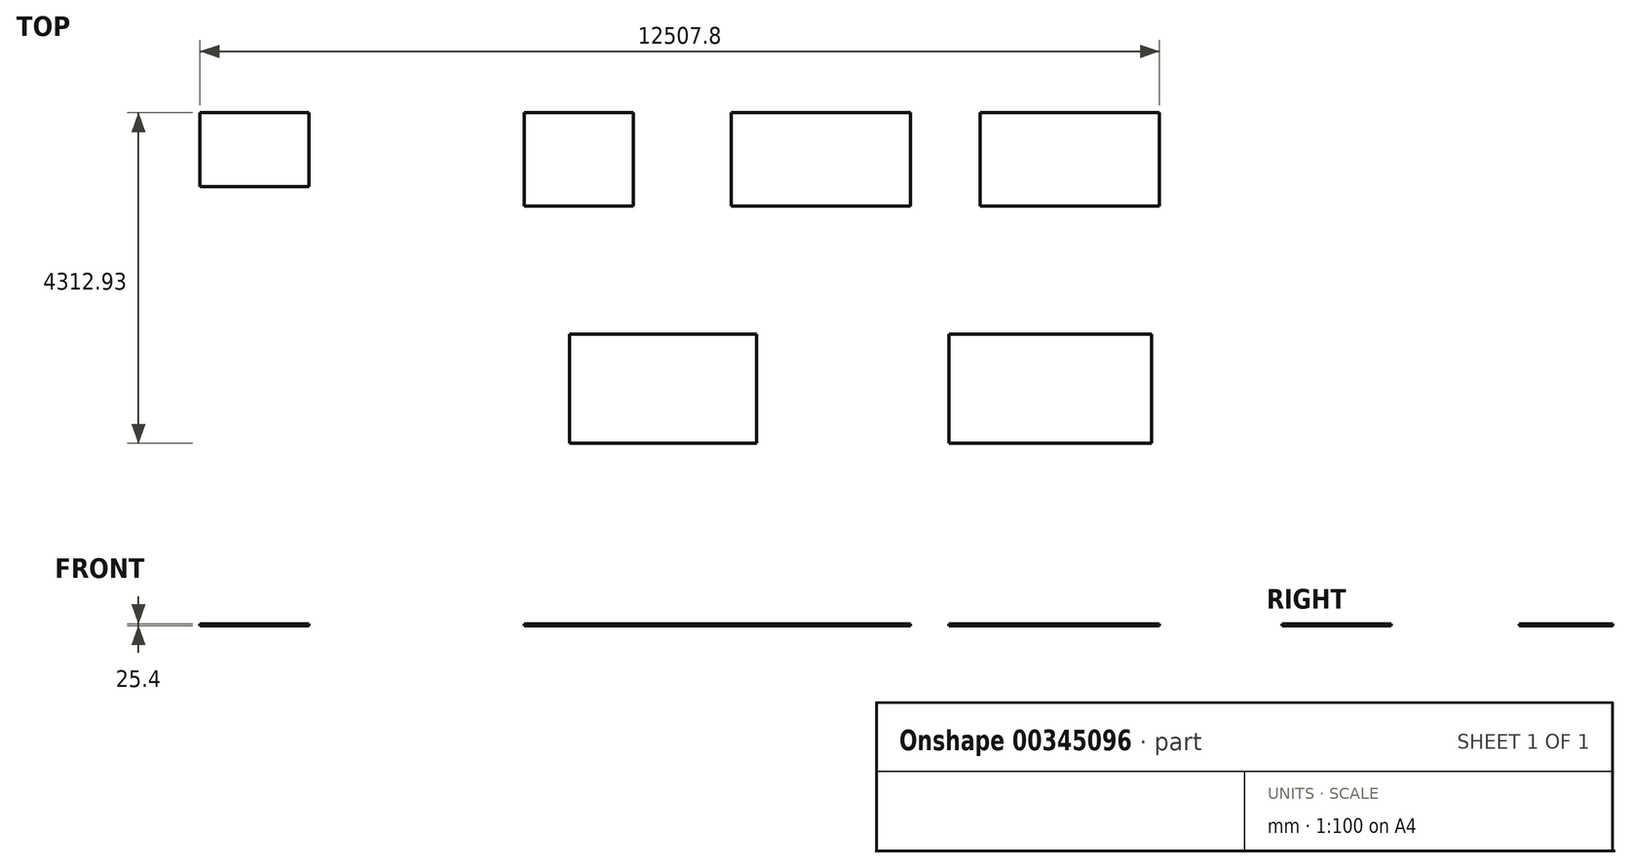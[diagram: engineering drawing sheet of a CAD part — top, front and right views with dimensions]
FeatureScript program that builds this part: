
annotation { "Feature Type Name" : "Feature", "Feature Type Description" : "" }
export const myFeature = defineFeature(function(context is Context, id is Id, definition is map)
    precondition{}
    {
        {
            var Q0;
            Q0=qCreatedBy(makeId("Top.planeOp"),FACE);
            var sketch = newSketch(context, id + "F0", { "sketchPlane" : qUnion([Q0])});
            skLineSegment(sketch, "E0.bottom", {"start": v(-2087.2, 1219.2) * mm, "end": v(351.2, 1219.2) * mm, "construction": true});
            skLineSegment(sketch, "E0.top", {"start": v(-2087.2, 0) * mm, "end": v(351.2, 0) * mm, "construction": true});
            skLineSegment(sketch, "E0.left", {"start": v(-2087.2, 1219.2) * mm, "end": v(-2087.2, 0) * mm, "construction": true});
            skLineSegment(sketch, "E0.right", {"start": v(351.2, 1219.2) * mm, "end": v(351.2, 0) * mm, "construction": true});
            skLineSegment(sketch, "E1.bottom", {"start": v(-2493.6, -1671.33) * mm, "end": v(351.2, -1671.33) * mm, "construction": true});
            skLineSegment(sketch, "E1.top", {"start": v(-2493.6, -3093.73) * mm, "end": v(351.2, -3093.73) * mm, "construction": true});
            skLineSegment(sketch, "E1.left", {"start": v(-2493.6, -1671.33) * mm, "end": v(-2493.6, -3093.73) * mm, "construction": true});
            skLineSegment(sketch, "E1.right", {"start": v(351.2, -1671.33) * mm, "end": v(351.2, -3093.73) * mm, "construction": true});
            skLineSegment(sketch, "E2", {"start": v(-1369.66, -1671.33) * mm, "end": v(-1369.66, -3093.73) * mm, "construction": true});
            skLineSegment(sketch, "E3.bottom", {"start": v(-2493.6, -1671.33) * mm, "end": v(-1274.4, -1671.33) * mm});
            skLineSegment(sketch, "E3.top", {"start": v(-2493.6, -3093.73) * mm, "end": v(-1274.4, -3093.73) * mm});
            skLineSegment(sketch, "E3.left", {"start": v(-2493.6, -1671.33) * mm, "end": v(-2493.6, -3093.73) * mm});
            skLineSegment(sketch, "E3.right", {"start": v(-1274.4, -1671.33) * mm, "end": v(-1274.4, -3093.73) * mm});
            skLineSegment(sketch, "E4.bottom", {"start": v(-2087.2, 1219.2) * mm, "end": v(-664.8, 1219.2) * mm});
            skLineSegment(sketch, "E4.top", {"start": v(-2087.2, 0) * mm, "end": v(-664.8, 0) * mm});
            skLineSegment(sketch, "E4.left", {"start": v(-2087.2, 1219.2) * mm, "end": v(-2087.2, 0) * mm});
            skLineSegment(sketch, "E4.right", {"start": v(-664.8, 1219.2) * mm, "end": v(-664.8, 0) * mm});
            skLineSegment(sketch, "E5.bottom", {"start": v(-7440.47, -1671.33) * mm, "end": v(-4036.87, -1671.33) * mm, "construction": true});
            skLineSegment(sketch, "E5.top", {"start": v(-7440.47, -3093.73) * mm, "end": v(-4036.87, -3093.73) * mm, "construction": true});
            skLineSegment(sketch, "E5.left", {"start": v(-7440.47, -1671.33) * mm, "end": v(-7440.47, -3093.73) * mm, "construction": true});
            skLineSegment(sketch, "E5.right", {"start": v(-4036.87, -1671.33) * mm, "end": v(-4036.87, -3093.73) * mm, "construction": true});
            skLineSegment(sketch, "E6.bottom", {"start": v(-2895.85, 1219.2) * mm, "end": v(-5334.25, 1219.2) * mm, "construction": true});
            skLineSegment(sketch, "E6.top", {"start": v(-2895.85, 0) * mm, "end": v(-5334.25, 0) * mm, "construction": true});
            skLineSegment(sketch, "E6.left", {"start": v(-2895.85, 1219.2) * mm, "end": v(-2895.85, 0) * mm, "construction": true});
            skLineSegment(sketch, "E6.right", {"start": v(-5334.25, 1219.2) * mm, "end": v(-5334.25, 0) * mm, "construction": true});
            skLineSegment(sketch, "E7.bottom", {"start": v(-5334.25, 1219.2) * mm, "end": v(-3911.85, 1219.2) * mm});
            skLineSegment(sketch, "E7.top", {"start": v(-5334.25, 0) * mm, "end": v(-3911.85, 0) * mm});
            skLineSegment(sketch, "E7.left", {"start": v(-5334.25, 1219.2) * mm, "end": v(-5334.25, 0) * mm});
            skLineSegment(sketch, "E7.right", {"start": v(-3911.85, 1219.2) * mm, "end": v(-3911.85, 0) * mm});
            skLineSegment(sketch, "E8.bottom", {"start": v(-7440.47, -1671.33) * mm, "end": v(-6221.27, -1671.33) * mm});
            skLineSegment(sketch, "E8.top", {"start": v(-7440.47, -3093.73) * mm, "end": v(-6221.27, -3093.73) * mm});
            skLineSegment(sketch, "E8.left", {"start": v(-7440.47, -1671.33) * mm, "end": v(-7440.47, -3093.73) * mm});
            skLineSegment(sketch, "E8.right", {"start": v(-6221.27, -1671.33) * mm, "end": v(-6221.27, -3093.73) * mm});
            skLineSegment(sketch, "E9.bottom", {"start": v(-3911.85, 1219.2) * mm, "end": v(-3200.65, 1219.2) * mm});
            skLineSegment(sketch, "E9.top", {"start": v(-3911.85, 0) * mm, "end": v(-3200.65, 0) * mm});
            skLineSegment(sketch, "E9.right", {"start": v(-3200.65, 1219.2) * mm, "end": v(-3200.65, 0) * mm});
            skLineSegment(sketch, "E10.bottom", {"start": v(-6221.27, -1671.33) * mm, "end": v(-5002.07, -1671.33) * mm});
            skLineSegment(sketch, "E10.top", {"start": v(-6221.27, -2382.53) * mm, "end": v(-5002.07, -2382.53) * mm});
            skLineSegment(sketch, "E10.left", {"start": v(-6221.27, -1671.33) * mm, "end": v(-6221.27, -2382.53) * mm});
            skLineSegment(sketch, "E10.right", {"start": v(-5002.07, -1671.33) * mm, "end": v(-5002.07, -2382.53) * mm});
            skLineSegment(sketch, "E11.top", {"start": v(-6221.27, -3093.73) * mm, "end": v(-5002.07, -3093.73) * mm});
            skLineSegment(sketch, "E11.left", {"start": v(-6221.27, -2382.53) * mm, "end": v(-6221.27, -3093.73) * mm});
            skLineSegment(sketch, "E11.right", {"start": v(-5002.07, -2382.53) * mm, "end": v(-5002.07, -3093.73) * mm});
            skLineSegment(sketch, "E12.bottom", {"start": v(-664.8, 1219.2) * mm, "end": v(46.4, 1219.2) * mm});
            skLineSegment(sketch, "E12.top", {"start": v(-664.8, 0) * mm, "end": v(46.4, 0) * mm});
            skLineSegment(sketch, "E12.right", {"start": v(46.4, 1219.2) * mm, "end": v(46.4, 0) * mm});
            skLineSegment(sketch, "E13.bottom", {"start": v(-5590.97, 1219.2) * mm, "end": v(-8029.37, 1219.2) * mm, "construction": true});
            skLineSegment(sketch, "E13.top", {"start": v(-5590.97, 0) * mm, "end": v(-8029.37, 0) * mm, "construction": true});
            skLineSegment(sketch, "E13.left", {"start": v(-5590.97, 1219.2) * mm, "end": v(-5590.97, 0) * mm, "construction": true});
            skLineSegment(sketch, "E13.right", {"start": v(-8029.37, 1219.2) * mm, "end": v(-8029.37, 0) * mm, "construction": true});
            skLineSegment(sketch, "E14.bottom", {"start": v(-8029.37, 1219.2) * mm, "end": v(-6606.97, 1219.2) * mm});
            skLineSegment(sketch, "E14.top", {"start": v(-8029.37, 0) * mm, "end": v(-6606.97, 0) * mm});
            skLineSegment(sketch, "E14.left", {"start": v(-8029.37, 1219.2) * mm, "end": v(-8029.37, 0) * mm});
            skLineSegment(sketch, "E14.right", {"start": v(-6606.97, 1219.2) * mm, "end": v(-6606.97, 0) * mm});
            skLineSegment(sketch, "E15.bottom", {"start": v(-1274.4, -1671.33) * mm, "end": v(148, -1671.33) * mm});
            skLineSegment(sketch, "E15.top", {"start": v(-1274.4, -3093.73) * mm, "end": v(148, -3093.73) * mm});
            skLineSegment(sketch, "E15.right", {"start": v(148, -1671.33) * mm, "end": v(148, -3093.73) * mm});
            skLineSegment(sketch, "E16.bottom", {"start": v(-9819.8, 1219.2) * mm, "end": v(-12258.2, 1219.2) * mm, "construction": true});
            skLineSegment(sketch, "E16.top", {"start": v(-9819.8, 0) * mm, "end": v(-12258.2, 0) * mm, "construction": true});
            skLineSegment(sketch, "E16.left", {"start": v(-9819.8, 1219.2) * mm, "end": v(-9819.8, 0) * mm, "construction": true});
            skLineSegment(sketch, "E16.right", {"start": v(-12258.2, 1219.2) * mm, "end": v(-12258.2, 0) * mm, "construction": true});
            skLineSegment(sketch, "E17.bottom", {"start": v(-12258.2, 1219.2) * mm, "end": v(-10835.8, 1219.2) * mm});
            skLineSegment(sketch, "E17.top", {"start": v(-12258.2, 254) * mm, "end": v(-10835.8, 254) * mm});
            skLineSegment(sketch, "E17.left", {"start": v(-12258.2, 1219.2) * mm, "end": v(-12258.2, 254) * mm});
            skLineSegment(sketch, "E17.right", {"start": v(-10835.8, 1219.2) * mm, "end": v(-10835.8, 254) * mm});
            skLineSegment(sketch, "E18.bottom", {"start": v(-3200.65, 1219.2) * mm, "end": v(-2997.45, 1219.2) * mm});
            skLineSegment(sketch, "E18.top", {"start": v(-3200.65, 0) * mm, "end": v(-2997.45, 0) * mm});
            skLineSegment(sketch, "E18.right", {"start": v(-2997.45, 1219.2) * mm, "end": v(-2997.45, 0) * mm});
            skLineSegment(sketch, "E19.bottom", {"start": v(46.4, 1219.2) * mm, "end": v(249.6, 1219.2) * mm});
            skLineSegment(sketch, "E19.top", {"start": v(46.4, 0) * mm, "end": v(249.6, 0) * mm});
            skLineSegment(sketch, "E19.right", {"start": v(249.6, 1219.2) * mm, "end": v(249.6, 0) * mm});
            skLineSegment(sketch, "E20", {"start": v(-5334.25, 609.6) * mm, "end": v(-3911.85, 609.6) * mm});
            skLineSegment(sketch, "E21", {"start": v(-2087.2, 609.6) * mm, "end": v(-664.8, 609.6) * mm});
            skLineSegment(sketch, "E22", {"start": v(-8029.37, 609.6) * mm, "end": v(-6606.97, 609.6) * mm});
            skLineSegment(sketch, "E23", {"start": v(-12258.2, 736.6) * mm, "end": v(-10835.8, 736.6) * mm});
            skLineSegment(sketch, "E24", {"start": v(-10835.8, 254) * mm, "end": v(-10835.8, 0) * mm});
            skSolve(sketch);
        }
        {
            var Q0;
            Q0 = qSketchRegion(id + "F0", true);
            extrude(context, id + "F1", {"entities" : qUnion([Q0]), "depth" : 25.4 * mm});
        }
    });
